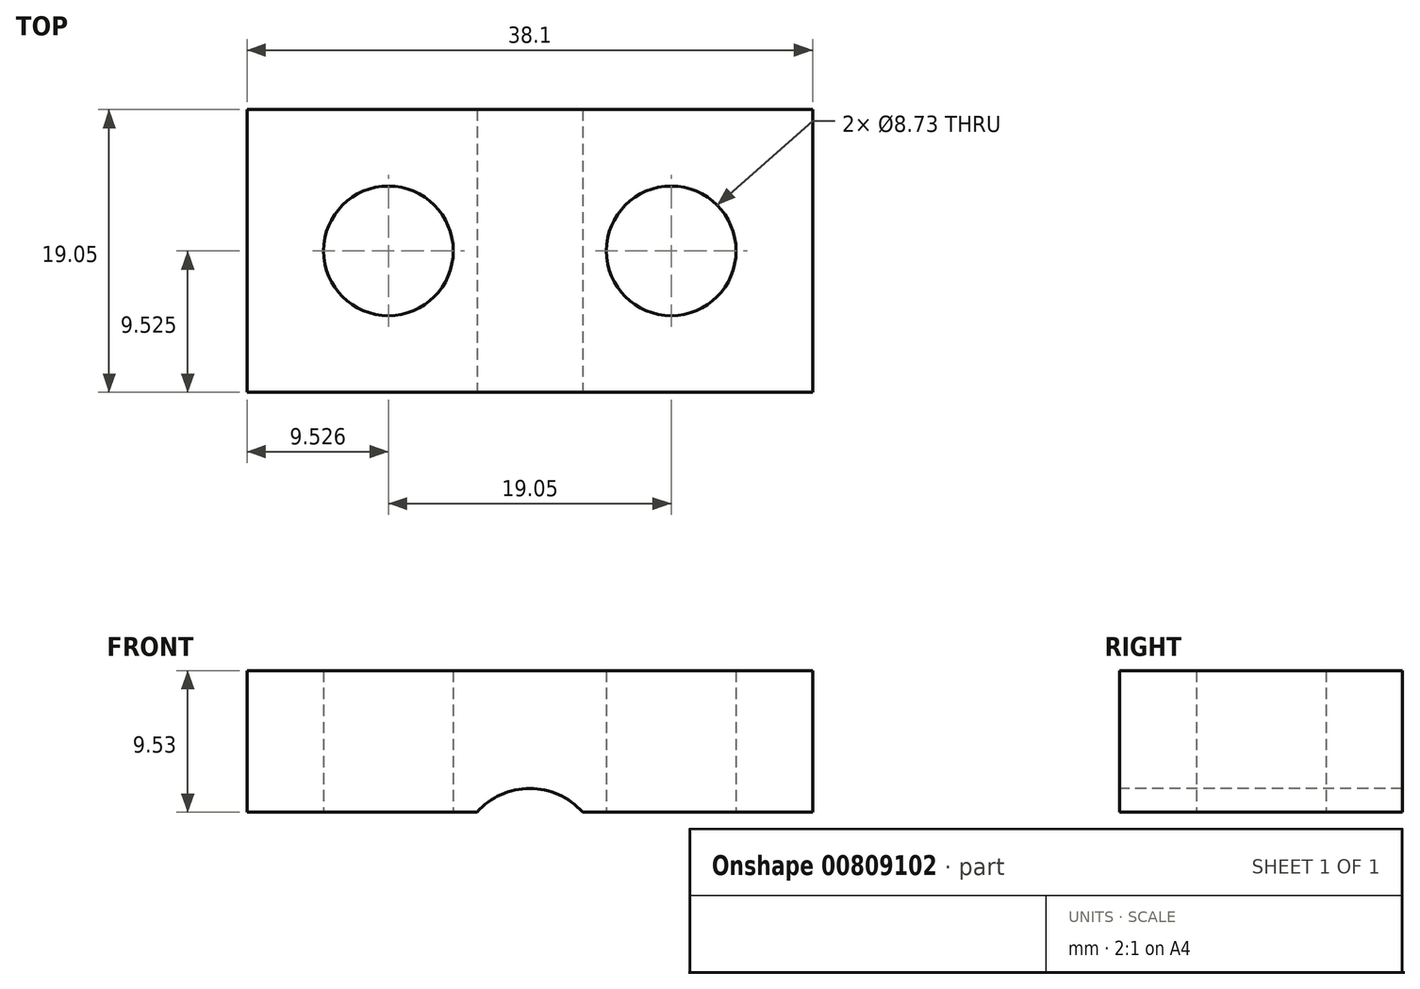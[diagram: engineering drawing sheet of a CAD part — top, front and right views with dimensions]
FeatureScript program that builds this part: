
annotation { "Feature Type Name" : "Feature", "Feature Type Description" : "" }
export const myFeature = defineFeature(function(context is Context, id is Id, definition is map)
    precondition{}
    {
        {
            var Q0;
            Q0=qCreatedBy(makeId("Top.planeOp"),FACE);
            var sketch = newSketch(context, id + "F0", { "sketchPlane" : qUnion([Q0])});
            skLineSegment(sketch, "E0.bottom", {"start": v(-4.92, 0) * mm, "end": v(33.18, 0) * mm});
            skLineSegment(sketch, "E0.top", {"start": v(-4.92, 19.05) * mm, "end": v(33.18, 19.05) * mm});
            skLineSegment(sketch, "E0.left", {"start": v(-4.92, 0) * mm, "end": v(-4.92, 19.05) * mm});
            skLineSegment(sketch, "E0.right", {"start": v(33.18, 0) * mm, "end": v(33.18, 19.05) * mm});
            skCircle(sketch, "E1", {"center": v(4.6, 9.52) * mm, "radius": 4.37 * mm});
            skPoint(sketch, "E1.centerSnap0", {"position": v(-4.92, 9.52) * mm});
            skCircle(sketch, "E2.1.0.0", {"center": v(23.66, 9.52) * mm, "radius": 4.37 * mm});
            skLineSegment(sketch, "E2.direction1", {"start": v(4.6, 9.52) * mm, "end": v(23.66, 9.52) * mm, "construction": true});
            skSolve(sketch);
        }
        {
            var Q0;
            Q0 = qSketchRegion(id + "F0", true);
            extrude(context, id + "F1", {"entities" : qUnion([Q0]), "depth" : 9.52 * mm, "offsetDistance" : 25.4 * mm});
        }
        {
            var Q0;
            Q0=makeQuery(id+"F1.opExtrude","SWEPT_FACE",FACE,{"disambiguationData":[OSD([sQuery(id+"F0.wireOp",EDGE,"E0.bottom")])]});
            var sketch = newSketch(context, id + "F2", { "sketchPlane" : qUnion([Q0])});
            skCircle(sketch, "E3", {"center": v(14.13, -3.18) * mm, "radius": 4.76 * mm});
            skPoint(sketch, "E3.centerSnap0", {"position": v(14.13, 0) * mm});
            skSolve(sketch);
        }
        {
            var Q0;
            Q0 = qSketchRegion(id + "F2", true);
            extrude(context, id + "F3", {"entities" : qUnion([Q0]), "operationType" : NewBodyOperationType.REMOVE, "oppositeDirection" : true, "depth" : 25.4 * mm, "offsetDistance" : 25.4 * mm});
        }
    });
